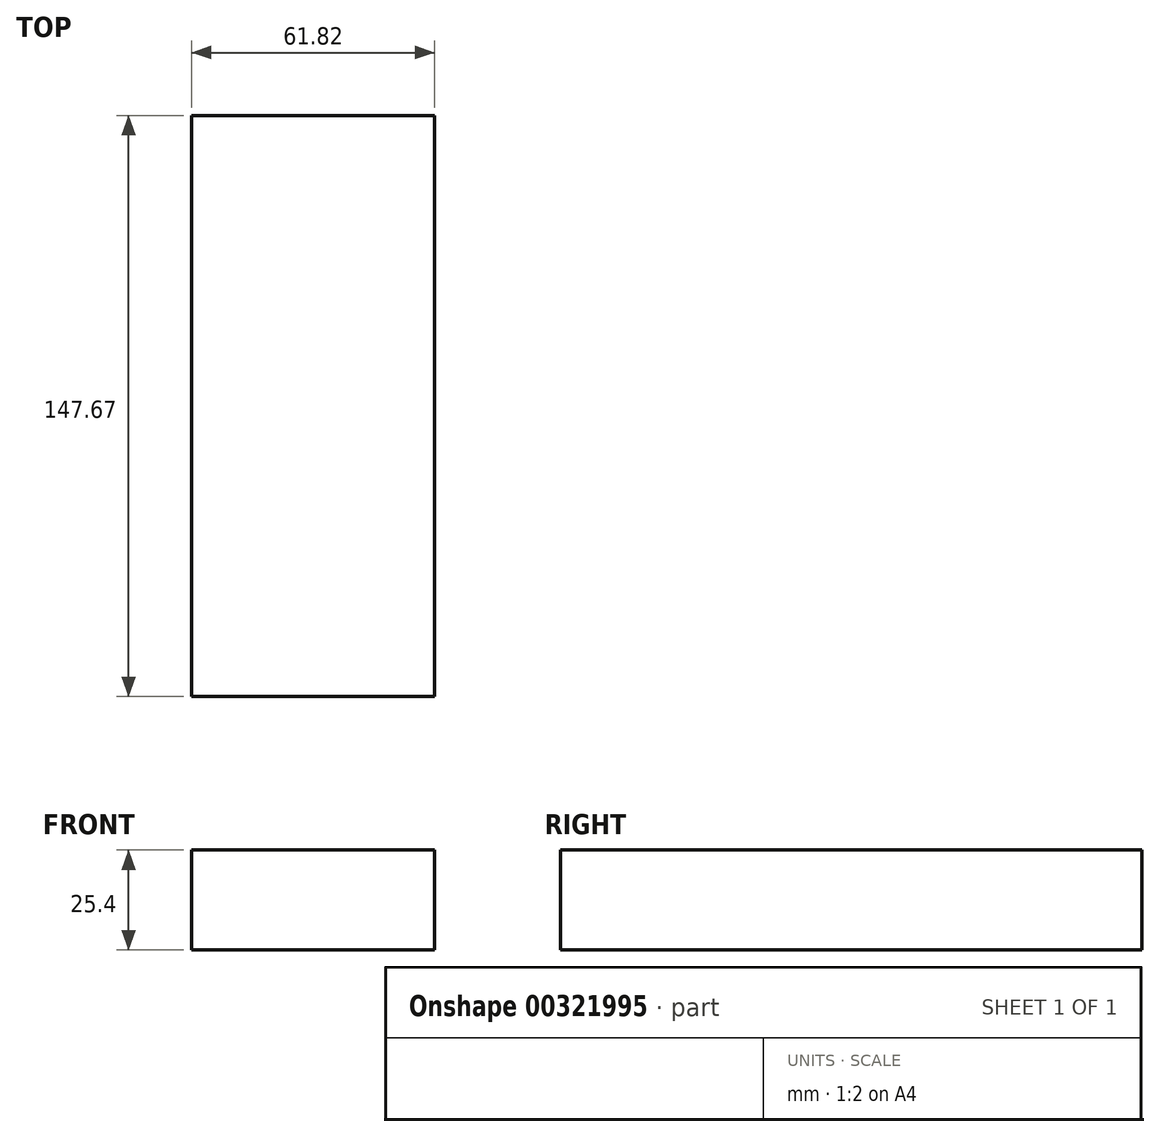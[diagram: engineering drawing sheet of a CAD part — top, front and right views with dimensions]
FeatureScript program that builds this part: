
annotation { "Feature Type Name" : "Feature", "Feature Type Description" : "" }
export const myFeature = defineFeature(function(context is Context, id is Id, definition is map)
    precondition{}
    {
        {
            var Q0;
            Q0=qCreatedBy(makeId("Top.planeOp"),FACE);
            var sketch = newSketch(context, id + "F0", { "sketchPlane" : qUnion([Q0])});
            skLineSegment(sketch, "E0.bottom", {"start": v(37.28, -98.42) * mm, "end": v(-24.54, -98.42) * mm});
            skLineSegment(sketch, "E0.top", {"start": v(37.28, 49.25) * mm, "end": v(-24.54, 49.25) * mm});
            skLineSegment(sketch, "E0.left", {"start": v(37.28, -98.42) * mm, "end": v(37.28, 49.25) * mm});
            skLineSegment(sketch, "E0.right", {"start": v(-24.54, -98.42) * mm, "end": v(-24.54, 49.25) * mm});
            skSolve(sketch);
        }
        {
            var Q0;
            Q0=makeQuery(id+"F0.imprint","IMPRINT",FACE,{"disambiguationData":[TD([[makeQuery(id+"F0.imprint","IMPRINT",EDGE,{"derivedFrom":sQuery(id+"F0.wireOp",EDGE,"E0.bottom")}),-1.0]])]});
            extrude(context, id + "F1", {"entities" : qUnion([Q0]), "depth" : 25.4 * mm});
        }
    });
